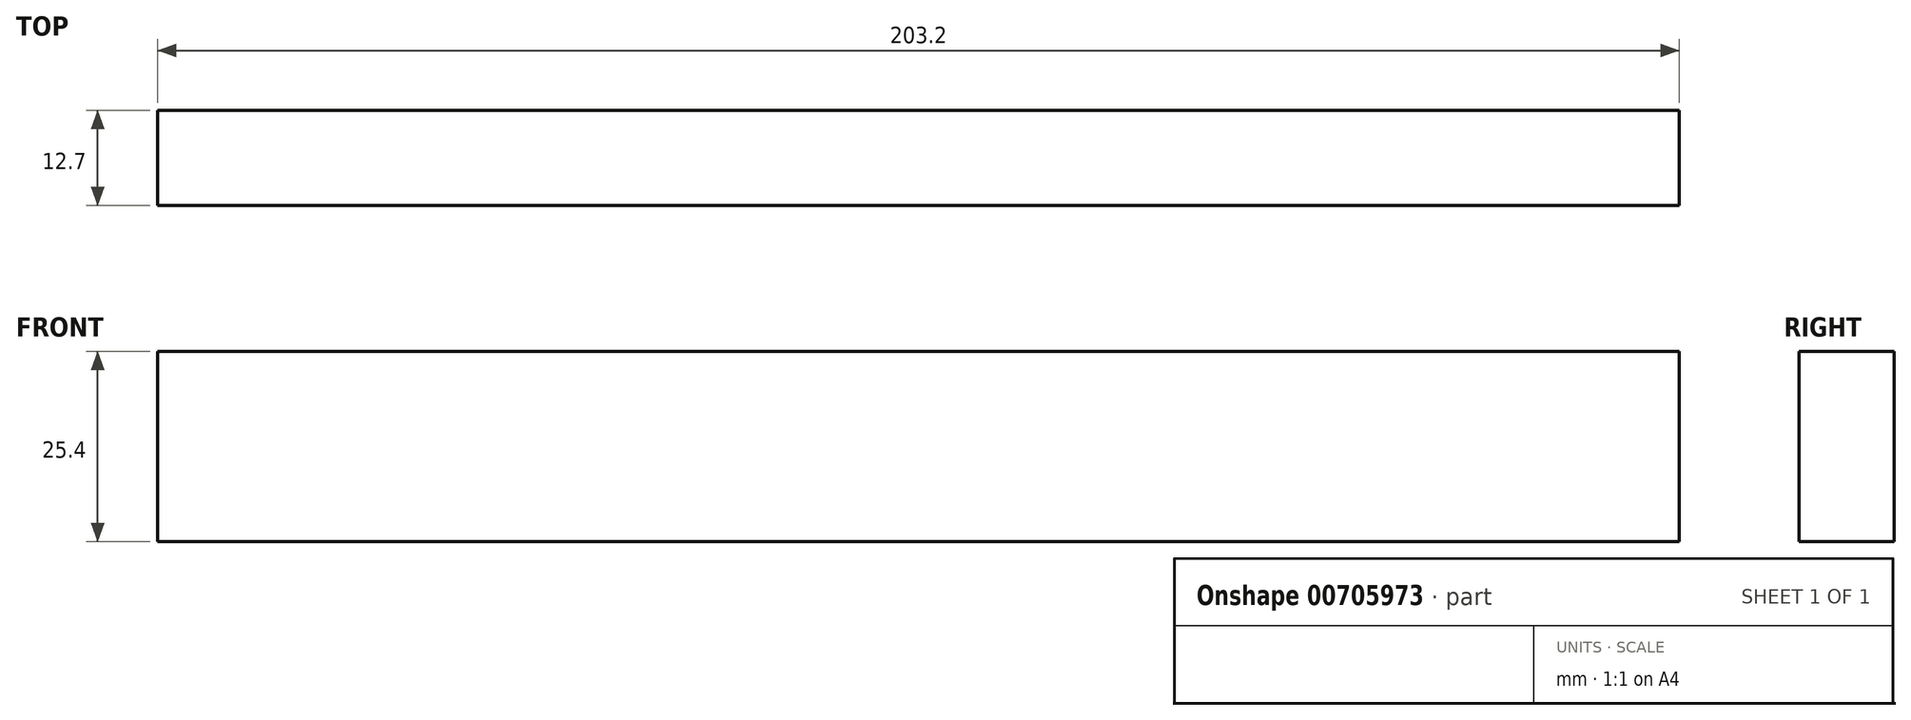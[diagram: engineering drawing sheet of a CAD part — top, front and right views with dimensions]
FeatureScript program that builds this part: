
annotation { "Feature Type Name" : "Feature", "Feature Type Description" : "" }
export const myFeature = defineFeature(function(context is Context, id is Id, definition is map)
    precondition{}
    {
        {
            var Q0;
            Q0=qCreatedBy(makeId("Top.planeOp"),FACE);
            var sketch = newSketch(context, id + "F0", { "sketchPlane" : qUnion([Q0])});
            skLineSegment(sketch, "E0.bottom", {"start": v(-45.14, 64.3) * mm, "end": v(158.06, 64.3) * mm});
            skLineSegment(sketch, "E0.top", {"start": v(-45.14, 51.6) * mm, "end": v(158.06, 51.6) * mm});
            skLineSegment(sketch, "E0.left", {"start": v(-45.14, 64.3) * mm, "end": v(-45.14, 51.6) * mm});
            skLineSegment(sketch, "E0.right", {"start": v(158.06, 64.3) * mm, "end": v(158.06, 51.6) * mm});
            skSolve(sketch);
        }
        {
            var Q0;
            Q0 = qSketchRegion(id + "F0", true);
            extrude(context, id + "F1", {"entities" : qUnion([Q0]), "depth" : 25.4 * mm, "offsetDistance" : 25.4 * mm});
        }
    });
